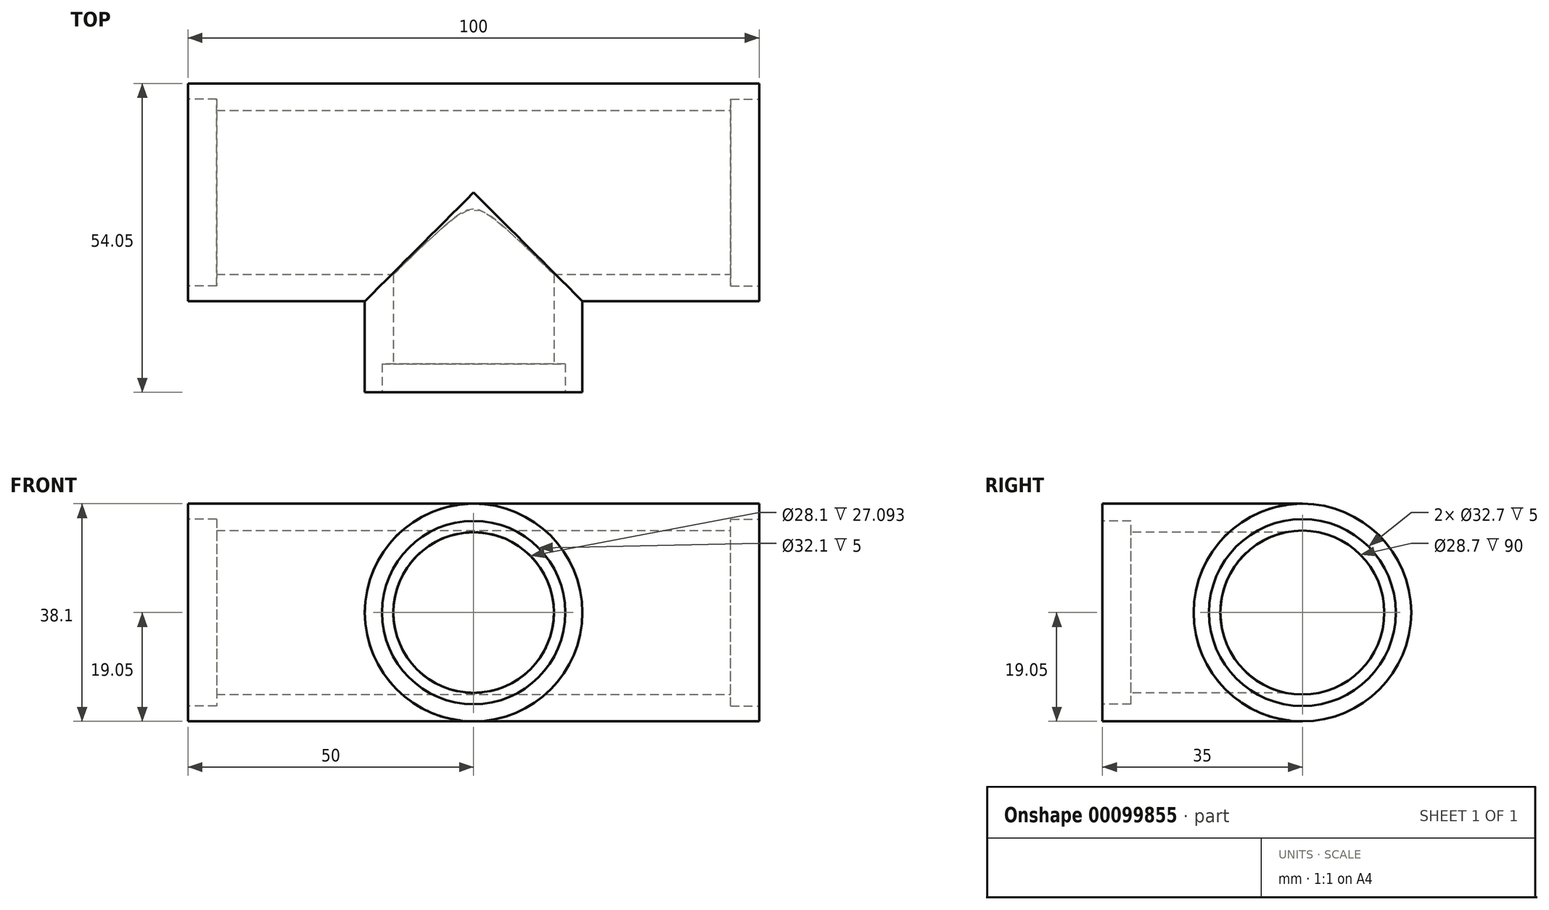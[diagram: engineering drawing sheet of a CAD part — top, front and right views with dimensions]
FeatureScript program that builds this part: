
annotation { "Feature Type Name" : "Feature", "Feature Type Description" : "" }
export const myFeature = defineFeature(function(context is Context, id is Id, definition is map)
    precondition{}
    {
        {
            var Q0;
            Q0=qCreatedBy(makeId("Right.planeOp"),FACE);
            var sketch = newSketch(context, id + "F0", { "sketchPlane" : qUnion([Q0])});
            skCircle(sketch, "E0", {"center": v(0, 0) * mm, "radius": 19.05 * mm});
            skSolve(sketch);
        }
        {
            var Q0;
            Q0=qCreatedBy(makeId("Front.planeOp"),FACE);
            var sketch = newSketch(context, id + "F1", { "sketchPlane" : qUnion([Q0])});
            skCircle(sketch, "E1", {"center": v(0, 0) * mm, "radius": 19.05 * mm});
            skLineSegment(sketch, "E2", {"start": v(-50, 19.05) * mm, "end": v(50, 19.05) * mm, "construction": true});
            skSolve(sketch);
        }
        {
            var Q0;
            Q0=qSketchRegion(id+"F0",true);
            extrude(context, id + "F2", {"entities" : qUnion([Q0]), "endBound" : BoundingType.SYMMETRIC, "depth" : 100 * mm});
        }
        {
            var Q0;
            Q0=makeQuery(id+"F2.opExtrude","CAP_FACE",FACE,{"disambiguationData":[OSD([sQuery(id+"F0.wireOp",EDGE,"E0")])],"isStart":false});
            var sketch = newSketch(context, id + "F3", { "sketchPlane" : qUnion([Q0])});
            skCircle(sketch, "E3", {"center": v(0, 0) * mm, "radius": 14.35 * mm});
            skSolve(sketch);
        }
        {
            var Q0;
            Q0=qSketchRegion(id+"F1",true);
            extrude(context, id + "F4", {"entities" : qUnion([Q0]), "operationType" : NewBodyOperationType.ADD, "depth" : 35 * mm});
        }
        {
            var Q0;
            Q0=qSketchRegion(id+"F3",true);
            extrude(context, id + "F5", {"entities" : qUnion([Q0]), "operationType" : NewBodyOperationType.REMOVE, "endBound" : BoundingType.THROUGH_ALL, "oppositeDirection" : true, "depth" : 25 * mm});
        }
        {
            var Q0;
            Q0=makeQuery(id+"F4.opExtrude","CAP_FACE",FACE,{"disambiguationData":[OSD([sQuery(id+"F1.wireOp",EDGE,"E1")])],"isStart":false});
            var sketch = newSketch(context, id + "F6", { "sketchPlane" : qUnion([Q0])});
            skCircle(sketch, "E4", {"center": v(0, 0) * mm, "radius": 14.05 * mm});
            skSolve(sketch);
        }
        {
            var Q0;
            Q0=qSketchRegion(id+"F6",true);
            extrude(context, id + "F7", {"entities" : qUnion([Q0]), "operationType" : NewBodyOperationType.REMOVE, "endBound" : BoundingType.UP_TO_NEXT, "oppositeDirection" : true, "depth" : 25 * mm});
        }
        {
            var Q0;
            Q0=makeQuery(id+"F4.opExtrude","CAP_FACE",FACE,{"disambiguationData":[OSD([sQuery(id+"F1.wireOp",EDGE,"E1")])],"isStart":false});
            var sketch = newSketch(context, id + "F8", { "sketchPlane" : qUnion([Q0])});
            skCircle(sketch, "E5", {"center": v(0, 0) * mm, "radius": 16.05 * mm});
            skSolve(sketch);
        }
        {
            var Q0;
            Q0=qSketchRegion(id+"F8",true);
            extrude(context, id + "F9", {"entities" : qUnion([Q0]), "operationType" : NewBodyOperationType.REMOVE, "oppositeDirection" : true, "depth" : 5 * mm});
        }
        {
            var Q0;
            Q0=makeQuery(id+"F2.opExtrude","CAP_FACE",FACE,{"disambiguationData":[OSD([sQuery(id+"F0.wireOp",EDGE,"E0")])],"isStart":false});
            var sketch = newSketch(context, id + "F10", { "sketchPlane" : qUnion([Q0])});
            skCircle(sketch, "E6", {"center": v(0, 0) * mm, "radius": 16.35 * mm});
            skSolve(sketch);
        }
        {
            var Q0;
            Q0=qSketchRegion(id+"F10",true);
            extrude(context, id + "F11", {"entities" : qUnion([Q0]), "operationType" : NewBodyOperationType.REMOVE, "oppositeDirection" : true, "depth" : 5 * mm});
        }
        {
            var Q0;
            Q0=makeQuery(id+"F2.opExtrude","CAP_FACE",FACE,{"disambiguationData":[OSD([sQuery(id+"F0.wireOp",EDGE,"E0")])],"isStart":true});
            var sketch = newSketch(context, id + "F12", { "sketchPlane" : qUnion([Q0])});
            skCircle(sketch, "E7", {"center": v(0, 0) * mm, "radius": 16.35 * mm});
            skSolve(sketch);
        }
        {
            var Q0;
            Q0=qSketchRegion(id+"F12",true);
            extrude(context, id + "F13", {"entities" : qUnion([Q0]), "operationType" : NewBodyOperationType.REMOVE, "oppositeDirection" : true, "depth" : 5 * mm});
        }
    });
